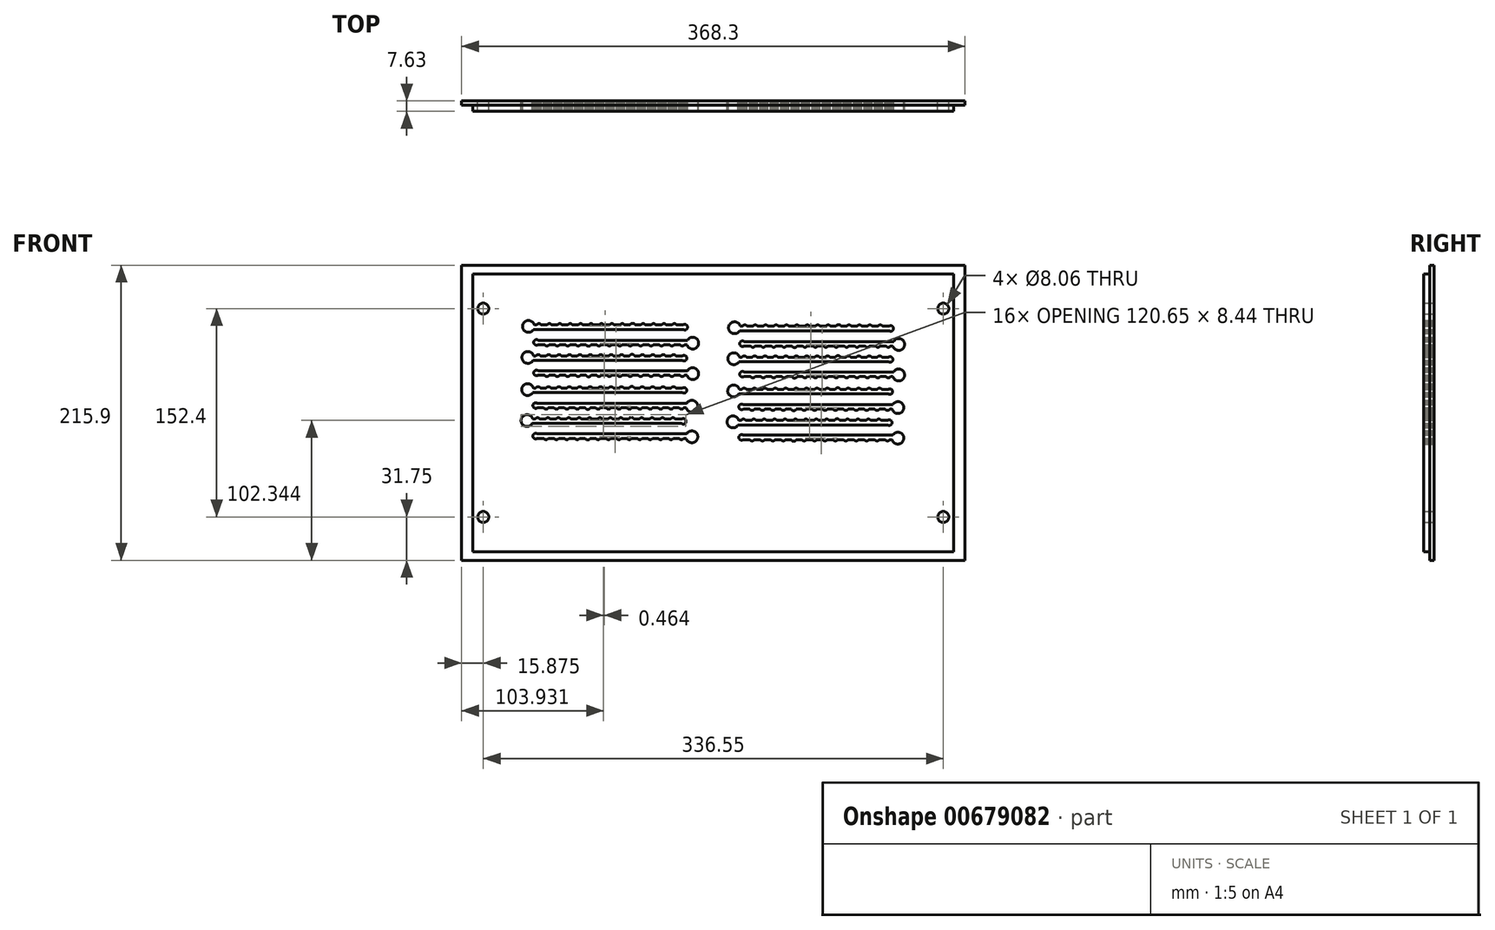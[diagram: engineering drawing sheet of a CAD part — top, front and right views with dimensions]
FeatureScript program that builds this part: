
annotation { "Feature Type Name" : "Feature", "Feature Type Description" : "" }
export const myFeature = defineFeature(function(context is Context, id is Id, definition is map)
    precondition{}
    {
        {
            var Q0;
            Q0=qCreatedBy(makeId("Front.planeOp"),FACE);
            var sketch = newSketch(context, id + "F0", { "sketchPlane" : qUnion([Q0])});
            skLineSegment(sketch, "E0.bottom", {"start": v(-184.15, 107.95) * mm, "end": v(184.15, 107.95) * mm});
            skLineSegment(sketch, "E0.top", {"start": v(-184.15, -107.95) * mm, "end": v(184.15, -107.95) * mm});
            skLineSegment(sketch, "E0.left", {"start": v(-184.15, 107.95) * mm, "end": v(-184.15, -107.95) * mm});
            skLineSegment(sketch, "E0.right", {"start": v(184.15, 107.95) * mm, "end": v(184.15, -107.95) * mm});
            skLineSegment(sketch, "E1.bottom", {"start": v(-175.9, 101.6) * mm, "end": v(175.9, 101.6) * mm});
            skLineSegment(sketch, "E1.top", {"start": v(-175.9, -101.6) * mm, "end": v(175.9, -101.6) * mm});
            skLineSegment(sketch, "E1.left", {"start": v(-175.9, 101.6) * mm, "end": v(-175.9, -101.6) * mm});
            skLineSegment(sketch, "E1.right", {"start": v(175.9, 101.6) * mm, "end": v(175.9, -101.6) * mm});
            skCircle(sketch, "E2", {"center": v(168.28, 76.2) * mm, "radius": 4.03 * mm});
            skCircle(sketch, "E3", {"center": v(168.28, -76.2) * mm, "radius": 4.03 * mm});
            skCircle(sketch, "E4", {"center": v(-168.28, -76.2) * mm, "radius": 4.03 * mm});
            skCircle(sketch, "E5", {"center": v(-168.28, 76.2) * mm, "radius": 4.03 * mm});
            skCircle(sketch, "E6", {"center": v(135.65, 50) * mm, "radius": 4.34 * mm});
            skCircle(sketch, "E7", {"center": v(128.03, 50) * mm, "radius": 2.05 * mm});
            skCircle(sketch, "E8", {"center": v(120.4, 50) * mm, "radius": 2.05 * mm});
            skCircle(sketch, "E9", {"center": v(112.79, 50) * mm, "radius": 2.05 * mm});
            skCircle(sketch, "E10", {"center": v(105.17, 50) * mm, "radius": 2.05 * mm});
            skCircle(sketch, "E11", {"center": v(97.55, 50) * mm, "radius": 2.05 * mm});
            skCircle(sketch, "E12", {"center": v(89.93, 50) * mm, "radius": 2.05 * mm});
            skCircle(sketch, "E13", {"center": v(82.3, 50) * mm, "radius": 2.05 * mm});
            skCircle(sketch, "E14", {"center": v(74.69, 50) * mm, "radius": 2.05 * mm});
            skCircle(sketch, "E15", {"center": v(67.07, 50) * mm, "radius": 2.05 * mm});
            skCircle(sketch, "E16", {"center": v(59.45, 49.73) * mm, "radius": 2.05 * mm});
            skCircle(sketch, "E17", {"center": v(51.83, 50) * mm, "radius": 2.05 * mm});
            skCircle(sketch, "E18", {"center": v(44.2, 50) * mm, "radius": 2.05 * mm});
            skCircle(sketch, "E19", {"center": v(36.59, 50) * mm, "radius": 2.05 * mm});
            skCircle(sketch, "E20", {"center": v(28.97, 50) * mm, "radius": 2.05 * mm});
            skCircle(sketch, "E21", {"center": v(21.35, 50.53) * mm, "radius": 2.05 * mm});
            skLineSegment(sketch, "E22", {"start": v(139.85, 48.92) * mm, "end": v(20.08, 48.92) * mm});
            skLineSegment(sketch, "E23", {"start": v(20.08, 48.92) * mm, "end": v(20.08, 52.14) * mm});
            skLineSegment(sketch, "E24", {"start": v(20.08, 52.14) * mm, "end": v(139.42, 52.14) * mm});
            skLineSegment(sketch, "E25", {"start": v(139.42, 52.14) * mm, "end": v(139.85, 48.92) * mm});
            skCircle(sketch, "E26", {"center": v(15.03, 39.53) * mm, "radius": 4.34 * mm});
            skCircle(sketch, "E27", {"center": v(22.65, 39.53) * mm, "radius": 2.05 * mm});
            skCircle(sketch, "E28", {"center": v(30.27, 39.53) * mm, "radius": 2.05 * mm});
            skCircle(sketch, "E29", {"center": v(37.89, 39.53) * mm, "radius": 2.05 * mm});
            skCircle(sketch, "E30", {"center": v(45.5, 39.53) * mm, "radius": 2.05 * mm});
            skCircle(sketch, "E31", {"center": v(53.13, 39.53) * mm, "radius": 2.05 * mm});
            skCircle(sketch, "E32", {"center": v(60.75, 39.53) * mm, "radius": 2.05 * mm});
            skCircle(sketch, "E33", {"center": v(68.37, 39.53) * mm, "radius": 2.05 * mm});
            skCircle(sketch, "E34", {"center": v(75.99, 39.53) * mm, "radius": 2.05 * mm});
            skCircle(sketch, "E35", {"center": v(83.6, 39.53) * mm, "radius": 2.05 * mm});
            skCircle(sketch, "E36", {"center": v(91.23, 39.8) * mm, "radius": 2.05 * mm});
            skCircle(sketch, "E37", {"center": v(98.85, 39.53) * mm, "radius": 2.05 * mm});
            skCircle(sketch, "E38", {"center": v(106.47, 39.53) * mm, "radius": 2.05 * mm});
            skCircle(sketch, "E39", {"center": v(114.09, 39.53) * mm, "radius": 2.05 * mm});
            skCircle(sketch, "E40", {"center": v(121.7, 39.53) * mm, "radius": 2.05 * mm});
            skCircle(sketch, "E41", {"center": v(129.33, 39) * mm, "radius": 2.05 * mm});
            skLineSegment(sketch, "E42", {"start": v(10.83, 40.61) * mm, "end": v(130.6, 40.61) * mm});
            skLineSegment(sketch, "E43", {"start": v(130.6, 40.61) * mm, "end": v(130.6, 37.39) * mm});
            skLineSegment(sketch, "E44", {"start": v(130.6, 37.39) * mm, "end": v(11.26, 37.39) * mm});
            skLineSegment(sketch, "E45", {"start": v(11.26, 37.39) * mm, "end": v(10.83, 40.61) * mm});
            skCircle(sketch, "E46", {"center": v(135.65, 27.67) * mm, "radius": 4.34 * mm});
            skCircle(sketch, "E47", {"center": v(128.03, 27.67) * mm, "radius": 2.05 * mm});
            skCircle(sketch, "E48", {"center": v(120.4, 27.67) * mm, "radius": 2.05 * mm});
            skCircle(sketch, "E49", {"center": v(112.79, 27.67) * mm, "radius": 2.05 * mm});
            skCircle(sketch, "E50", {"center": v(105.17, 27.67) * mm, "radius": 2.05 * mm});
            skCircle(sketch, "E51", {"center": v(97.55, 27.67) * mm, "radius": 2.05 * mm});
            skCircle(sketch, "E52", {"center": v(89.93, 27.67) * mm, "radius": 2.05 * mm});
            skCircle(sketch, "E53", {"center": v(82.3, 27.67) * mm, "radius": 2.05 * mm});
            skCircle(sketch, "E54", {"center": v(74.69, 27.67) * mm, "radius": 2.05 * mm});
            skCircle(sketch, "E55", {"center": v(67.07, 27.67) * mm, "radius": 2.05 * mm});
            skCircle(sketch, "E56", {"center": v(59.45, 27.4) * mm, "radius": 2.05 * mm});
            skCircle(sketch, "E57", {"center": v(51.83, 27.67) * mm, "radius": 2.05 * mm});
            skCircle(sketch, "E58", {"center": v(44.2, 27.67) * mm, "radius": 2.05 * mm});
            skCircle(sketch, "E59", {"center": v(36.59, 27.67) * mm, "radius": 2.05 * mm});
            skCircle(sketch, "E60", {"center": v(28.97, 27.67) * mm, "radius": 2.05 * mm});
            skCircle(sketch, "E61", {"center": v(21.35, 28.2) * mm, "radius": 2.05 * mm});
            skLineSegment(sketch, "E62", {"start": v(139.85, 26.59) * mm, "end": v(20.08, 26.59) * mm});
            skLineSegment(sketch, "E63", {"start": v(20.08, 26.59) * mm, "end": v(20.08, 29.8) * mm});
            skLineSegment(sketch, "E64", {"start": v(20.08, 29.8) * mm, "end": v(139.42, 29.8) * mm});
            skLineSegment(sketch, "E65", {"start": v(139.42, 29.8) * mm, "end": v(139.85, 26.59) * mm});
            skCircle(sketch, "E66", {"center": v(15.5, 62.2) * mm, "radius": 4.34 * mm});
            skCircle(sketch, "E67", {"center": v(23.11, 62.2) * mm, "radius": 2.05 * mm});
            skCircle(sketch, "E68", {"center": v(30.73, 62.2) * mm, "radius": 2.05 * mm});
            skCircle(sketch, "E69", {"center": v(38.35, 62.2) * mm, "radius": 2.05 * mm});
            skCircle(sketch, "E70", {"center": v(45.97, 62.2) * mm, "radius": 2.05 * mm});
            skCircle(sketch, "E71", {"center": v(53.6, 62.2) * mm, "radius": 2.05 * mm});
            skCircle(sketch, "E72", {"center": v(61.21, 62.2) * mm, "radius": 2.05 * mm});
            skCircle(sketch, "E73", {"center": v(68.83, 62.2) * mm, "radius": 2.05 * mm});
            skCircle(sketch, "E74", {"center": v(76.45, 62.2) * mm, "radius": 2.05 * mm});
            skCircle(sketch, "E75", {"center": v(84.07, 62.2) * mm, "radius": 2.05 * mm});
            skCircle(sketch, "E76", {"center": v(91.7, 62.47) * mm, "radius": 2.05 * mm});
            skCircle(sketch, "E77", {"center": v(99.31, 62.2) * mm, "radius": 2.05 * mm});
            skCircle(sketch, "E78", {"center": v(106.93, 62.2) * mm, "radius": 2.05 * mm});
            skCircle(sketch, "E79", {"center": v(114.55, 62.2) * mm, "radius": 2.05 * mm});
            skCircle(sketch, "E80", {"center": v(122.17, 62.2) * mm, "radius": 2.05 * mm});
            skCircle(sketch, "E81", {"center": v(129.8, 61.67) * mm, "radius": 2.05 * mm});
            skLineSegment(sketch, "E82", {"start": v(11.3, 63.28) * mm, "end": v(131.06, 63.28) * mm});
            skLineSegment(sketch, "E83", {"start": v(131.06, 63.28) * mm, "end": v(131.06, 60.06) * mm});
            skLineSegment(sketch, "E84", {"start": v(131.06, 60.06) * mm, "end": v(11.72, 60.06) * mm});
            skLineSegment(sketch, "E85", {"start": v(11.72, 60.06) * mm, "end": v(11.3, 63.28) * mm});
            skCircle(sketch, "E86", {"center": v(135.05, 3.79) * mm, "radius": 4.34 * mm});
            skCircle(sketch, "E87", {"center": v(127.43, 3.79) * mm, "radius": 2.05 * mm});
            skCircle(sketch, "E88", {"center": v(119.8, 3.79) * mm, "radius": 2.05 * mm});
            skCircle(sketch, "E89", {"center": v(112.19, 3.79) * mm, "radius": 2.05 * mm});
            skCircle(sketch, "E90", {"center": v(104.57, 3.79) * mm, "radius": 2.05 * mm});
            skCircle(sketch, "E91", {"center": v(96.95, 3.79) * mm, "radius": 2.05 * mm});
            skCircle(sketch, "E92", {"center": v(89.33, 3.79) * mm, "radius": 2.05 * mm});
            skCircle(sketch, "E93", {"center": v(81.7, 3.79) * mm, "radius": 2.05 * mm});
            skCircle(sketch, "E94", {"center": v(74.09, 3.79) * mm, "radius": 2.05 * mm});
            skCircle(sketch, "E95", {"center": v(66.47, 3.79) * mm, "radius": 2.05 * mm});
            skCircle(sketch, "E96", {"center": v(58.85, 3.52) * mm, "radius": 2.05 * mm});
            skCircle(sketch, "E97", {"center": v(51.23, 3.79) * mm, "radius": 2.05 * mm});
            skCircle(sketch, "E98", {"center": v(43.6, 3.79) * mm, "radius": 2.05 * mm});
            skCircle(sketch, "E99", {"center": v(35.99, 3.79) * mm, "radius": 2.05 * mm});
            skCircle(sketch, "E100", {"center": v(28.37, 3.79) * mm, "radius": 2.05 * mm});
            skCircle(sketch, "E101", {"center": v(20.75, 4.32) * mm, "radius": 2.05 * mm});
            skLineSegment(sketch, "E102", {"start": v(139.25, 2.71) * mm, "end": v(19.47, 2.71) * mm});
            skLineSegment(sketch, "E103", {"start": v(19.47, 2.71) * mm, "end": v(19.47, 5.93) * mm});
            skLineSegment(sketch, "E104", {"start": v(19.47, 5.93) * mm, "end": v(138.82, 5.93) * mm});
            skLineSegment(sketch, "E105", {"start": v(138.82, 5.93) * mm, "end": v(139.25, 2.71) * mm});
            skCircle(sketch, "E106", {"center": v(14.43, -6.68) * mm, "radius": 4.34 * mm});
            skCircle(sketch, "E107", {"center": v(22.05, -6.68) * mm, "radius": 2.05 * mm});
            skCircle(sketch, "E108", {"center": v(29.67, -6.68) * mm, "radius": 2.05 * mm});
            skCircle(sketch, "E109", {"center": v(37.29, -6.68) * mm, "radius": 2.05 * mm});
            skCircle(sketch, "E110", {"center": v(44.9, -6.68) * mm, "radius": 2.05 * mm});
            skCircle(sketch, "E111", {"center": v(52.53, -6.68) * mm, "radius": 2.05 * mm});
            skCircle(sketch, "E112", {"center": v(60.15, -6.68) * mm, "radius": 2.05 * mm});
            skCircle(sketch, "E113", {"center": v(67.77, -6.68) * mm, "radius": 2.05 * mm});
            skCircle(sketch, "E114", {"center": v(75.39, -6.68) * mm, "radius": 2.05 * mm});
            skCircle(sketch, "E115", {"center": v(83, -6.68) * mm, "radius": 2.05 * mm});
            skCircle(sketch, "E116", {"center": v(90.63, -6.4) * mm, "radius": 2.05 * mm});
            skCircle(sketch, "E117", {"center": v(98.25, -6.68) * mm, "radius": 2.05 * mm});
            skCircle(sketch, "E118", {"center": v(105.87, -6.68) * mm, "radius": 2.05 * mm});
            skCircle(sketch, "E119", {"center": v(113.49, -6.68) * mm, "radius": 2.05 * mm});
            skCircle(sketch, "E120", {"center": v(121.1, -6.68) * mm, "radius": 2.05 * mm});
            skCircle(sketch, "E121", {"center": v(128.73, -7.2) * mm, "radius": 2.05 * mm});
            skLineSegment(sketch, "E122", {"start": v(10.23, -5.6) * mm, "end": v(130, -5.6) * mm});
            skLineSegment(sketch, "E123", {"start": v(130, -5.6) * mm, "end": v(130, -8.82) * mm});
            skLineSegment(sketch, "E124", {"start": v(130, -8.82) * mm, "end": v(10.66, -8.82) * mm});
            skLineSegment(sketch, "E125", {"start": v(10.66, -8.82) * mm, "end": v(10.23, -5.6) * mm});
            skCircle(sketch, "E126", {"center": v(135.05, -18.54) * mm, "radius": 4.34 * mm});
            skCircle(sketch, "E127", {"center": v(127.43, -18.54) * mm, "radius": 2.05 * mm});
            skCircle(sketch, "E128", {"center": v(119.8, -18.54) * mm, "radius": 2.05 * mm});
            skCircle(sketch, "E129", {"center": v(112.19, -18.54) * mm, "radius": 2.05 * mm});
            skCircle(sketch, "E130", {"center": v(104.57, -18.54) * mm, "radius": 2.05 * mm});
            skCircle(sketch, "E131", {"center": v(96.95, -18.54) * mm, "radius": 2.05 * mm});
            skCircle(sketch, "E132", {"center": v(89.33, -18.54) * mm, "radius": 2.05 * mm});
            skCircle(sketch, "E133", {"center": v(81.7, -18.54) * mm, "radius": 2.05 * mm});
            skCircle(sketch, "E134", {"center": v(74.09, -18.54) * mm, "radius": 2.05 * mm});
            skCircle(sketch, "E135", {"center": v(66.47, -18.54) * mm, "radius": 2.05 * mm});
            skCircle(sketch, "E136", {"center": v(58.85, -18.8) * mm, "radius": 2.05 * mm});
            skCircle(sketch, "E137", {"center": v(51.23, -18.54) * mm, "radius": 2.05 * mm});
            skCircle(sketch, "E138", {"center": v(43.6, -18.54) * mm, "radius": 2.05 * mm});
            skCircle(sketch, "E139", {"center": v(35.99, -18.54) * mm, "radius": 2.05 * mm});
            skCircle(sketch, "E140", {"center": v(28.37, -18.54) * mm, "radius": 2.05 * mm});
            skCircle(sketch, "E141", {"center": v(20.75, -18) * mm, "radius": 2.05 * mm});
            skLineSegment(sketch, "E142", {"start": v(139.25, -19.62) * mm, "end": v(19.47, -19.62) * mm});
            skLineSegment(sketch, "E143", {"start": v(19.47, -19.62) * mm, "end": v(19.47, -16.4) * mm});
            skLineSegment(sketch, "E144", {"start": v(19.47, -16.4) * mm, "end": v(138.82, -16.4) * mm});
            skLineSegment(sketch, "E145", {"start": v(138.82, -16.4) * mm, "end": v(139.25, -19.62) * mm});
            skCircle(sketch, "E146", {"center": v(14.9, 16) * mm, "radius": 4.34 * mm});
            skCircle(sketch, "E147", {"center": v(22.51, 16) * mm, "radius": 2.05 * mm});
            skCircle(sketch, "E148", {"center": v(30.13, 16) * mm, "radius": 2.05 * mm});
            skCircle(sketch, "E149", {"center": v(37.75, 16) * mm, "radius": 2.05 * mm});
            skCircle(sketch, "E150", {"center": v(45.37, 16) * mm, "radius": 2.05 * mm});
            skCircle(sketch, "E151", {"center": v(53, 16) * mm, "radius": 2.05 * mm});
            skCircle(sketch, "E152", {"center": v(60.61, 16) * mm, "radius": 2.05 * mm});
            skCircle(sketch, "E153", {"center": v(68.23, 16) * mm, "radius": 2.05 * mm});
            skCircle(sketch, "E154", {"center": v(75.85, 16) * mm, "radius": 2.05 * mm});
            skCircle(sketch, "E155", {"center": v(83.47, 16) * mm, "radius": 2.05 * mm});
            skCircle(sketch, "E156", {"center": v(91.1, 16.26) * mm, "radius": 2.05 * mm});
            skCircle(sketch, "E157", {"center": v(98.71, 16) * mm, "radius": 2.05 * mm});
            skCircle(sketch, "E158", {"center": v(106.33, 16) * mm, "radius": 2.05 * mm});
            skCircle(sketch, "E159", {"center": v(113.95, 16) * mm, "radius": 2.05 * mm});
            skCircle(sketch, "E160", {"center": v(121.57, 16) * mm, "radius": 2.05 * mm});
            skCircle(sketch, "E161", {"center": v(129.2, 15.47) * mm, "radius": 2.05 * mm});
            skLineSegment(sketch, "E162", {"start": v(10.7, 17.08) * mm, "end": v(130.46, 17.08) * mm});
            skLineSegment(sketch, "E163", {"start": v(130.46, 17.08) * mm, "end": v(130.46, 13.86) * mm});
            skLineSegment(sketch, "E164", {"start": v(130.46, 13.86) * mm, "end": v(11.12, 13.86) * mm});
            skLineSegment(sketch, "E165", {"start": v(11.12, 13.86) * mm, "end": v(10.7, 17.08) * mm});
            skCircle(sketch, "E166", {"center": v(-15.03, 50.96) * mm, "radius": 4.34 * mm});
            skCircle(sketch, "E167", {"center": v(-22.65, 50.96) * mm, "radius": 2.05 * mm});
            skCircle(sketch, "E168", {"center": v(-30.27, 50.96) * mm, "radius": 2.05 * mm});
            skCircle(sketch, "E169", {"center": v(-37.89, 50.96) * mm, "radius": 2.05 * mm});
            skCircle(sketch, "E170", {"center": v(-45.5, 50.96) * mm, "radius": 2.05 * mm});
            skCircle(sketch, "E171", {"center": v(-53.13, 50.96) * mm, "radius": 2.05 * mm});
            skCircle(sketch, "E172", {"center": v(-60.75, 50.96) * mm, "radius": 2.05 * mm});
            skCircle(sketch, "E173", {"center": v(-68.37, 50.96) * mm, "radius": 2.05 * mm});
            skCircle(sketch, "E174", {"center": v(-75.99, 50.96) * mm, "radius": 2.05 * mm});
            skCircle(sketch, "E175", {"center": v(-83.6, 50.96) * mm, "radius": 2.05 * mm});
            skCircle(sketch, "E176", {"center": v(-91.23, 50.7) * mm, "radius": 2.05 * mm});
            skCircle(sketch, "E177", {"center": v(-98.85, 50.96) * mm, "radius": 2.05 * mm});
            skCircle(sketch, "E178", {"center": v(-106.47, 50.96) * mm, "radius": 2.05 * mm});
            skCircle(sketch, "E179", {"center": v(-114.09, 50.96) * mm, "radius": 2.05 * mm});
            skCircle(sketch, "E180", {"center": v(-121.7, 50.96) * mm, "radius": 2.05 * mm});
            skCircle(sketch, "E181", {"center": v(-129.33, 51.49) * mm, "radius": 2.05 * mm});
            skLineSegment(sketch, "E182", {"start": v(-10.83, 49.88) * mm, "end": v(-130.6, 49.88) * mm});
            skLineSegment(sketch, "E183", {"start": v(-130.6, 49.88) * mm, "end": v(-130.6, 53.1) * mm});
            skLineSegment(sketch, "E184", {"start": v(-130.6, 53.1) * mm, "end": v(-11.26, 53.1) * mm});
            skLineSegment(sketch, "E185", {"start": v(-11.26, 53.1) * mm, "end": v(-10.83, 49.88) * mm});
            skCircle(sketch, "E186", {"center": v(-135.64, 40.5) * mm, "radius": 4.34 * mm});
            skCircle(sketch, "E187", {"center": v(-128.02, 40.5) * mm, "radius": 2.05 * mm});
            skCircle(sketch, "E188", {"center": v(-120.4, 40.5) * mm, "radius": 2.05 * mm});
            skCircle(sketch, "E189", {"center": v(-112.78, 40.5) * mm, "radius": 2.05 * mm});
            skCircle(sketch, "E190", {"center": v(-105.16, 40.5) * mm, "radius": 2.05 * mm});
            skCircle(sketch, "E191", {"center": v(-97.54, 40.5) * mm, "radius": 2.05 * mm});
            skCircle(sketch, "E192", {"center": v(-89.92, 40.5) * mm, "radius": 2.05 * mm});
            skCircle(sketch, "E193", {"center": v(-82.3, 40.5) * mm, "radius": 2.05 * mm});
            skCircle(sketch, "E194", {"center": v(-74.68, 40.5) * mm, "radius": 2.05 * mm});
            skCircle(sketch, "E195", {"center": v(-67.06, 40.5) * mm, "radius": 2.05 * mm});
            skCircle(sketch, "E196", {"center": v(-59.44, 40.76) * mm, "radius": 2.05 * mm});
            skCircle(sketch, "E197", {"center": v(-51.82, 40.5) * mm, "radius": 2.05 * mm});
            skCircle(sketch, "E198", {"center": v(-44.2, 40.5) * mm, "radius": 2.05 * mm});
            skCircle(sketch, "E199", {"center": v(-36.58, 40.5) * mm, "radius": 2.05 * mm});
            skCircle(sketch, "E200", {"center": v(-28.96, 40.5) * mm, "radius": 2.05 * mm});
            skCircle(sketch, "E201", {"center": v(-21.34, 39.96) * mm, "radius": 2.05 * mm});
            skLineSegment(sketch, "E202", {"start": v(-139.85, 41.57) * mm, "end": v(-20.07, 41.57) * mm});
            skLineSegment(sketch, "E203", {"start": v(-20.07, 41.57) * mm, "end": v(-20.07, 38.35) * mm});
            skLineSegment(sketch, "E204", {"start": v(-20.07, 38.35) * mm, "end": v(-139.42, 38.35) * mm});
            skLineSegment(sketch, "E205", {"start": v(-139.42, 38.35) * mm, "end": v(-139.85, 41.57) * mm});
            skCircle(sketch, "E206", {"center": v(-15.03, 28.63) * mm, "radius": 4.34 * mm});
            skCircle(sketch, "E207", {"center": v(-22.65, 28.63) * mm, "radius": 2.05 * mm});
            skCircle(sketch, "E208", {"center": v(-30.27, 28.63) * mm, "radius": 2.05 * mm});
            skCircle(sketch, "E209", {"center": v(-37.89, 28.63) * mm, "radius": 2.05 * mm});
            skCircle(sketch, "E210", {"center": v(-45.5, 28.63) * mm, "radius": 2.05 * mm});
            skCircle(sketch, "E211", {"center": v(-53.13, 28.63) * mm, "radius": 2.05 * mm});
            skCircle(sketch, "E212", {"center": v(-60.75, 28.63) * mm, "radius": 2.05 * mm});
            skCircle(sketch, "E213", {"center": v(-68.37, 28.63) * mm, "radius": 2.05 * mm});
            skCircle(sketch, "E214", {"center": v(-75.99, 28.63) * mm, "radius": 2.05 * mm});
            skCircle(sketch, "E215", {"center": v(-83.6, 28.63) * mm, "radius": 2.05 * mm});
            skCircle(sketch, "E216", {"center": v(-91.23, 28.36) * mm, "radius": 2.05 * mm});
            skCircle(sketch, "E217", {"center": v(-98.85, 28.63) * mm, "radius": 2.05 * mm});
            skCircle(sketch, "E218", {"center": v(-106.47, 28.63) * mm, "radius": 2.05 * mm});
            skCircle(sketch, "E219", {"center": v(-114.09, 28.63) * mm, "radius": 2.05 * mm});
            skCircle(sketch, "E220", {"center": v(-121.7, 28.63) * mm, "radius": 2.05 * mm});
            skCircle(sketch, "E221", {"center": v(-129.33, 29.16) * mm, "radius": 2.05 * mm});
            skLineSegment(sketch, "E222", {"start": v(-10.83, 27.55) * mm, "end": v(-130.6, 27.55) * mm});
            skLineSegment(sketch, "E223", {"start": v(-130.6, 27.55) * mm, "end": v(-130.6, 30.77) * mm});
            skLineSegment(sketch, "E224", {"start": v(-130.6, 30.77) * mm, "end": v(-11.26, 30.77) * mm});
            skLineSegment(sketch, "E225", {"start": v(-11.26, 30.77) * mm, "end": v(-10.83, 27.55) * mm});
            skCircle(sketch, "E226", {"center": v(-135.18, 63.17) * mm, "radius": 4.34 * mm});
            skCircle(sketch, "E227", {"center": v(-127.56, 63.17) * mm, "radius": 2.05 * mm});
            skCircle(sketch, "E228", {"center": v(-119.94, 63.17) * mm, "radius": 2.05 * mm});
            skCircle(sketch, "E229", {"center": v(-112.32, 63.17) * mm, "radius": 2.05 * mm});
            skCircle(sketch, "E230", {"center": v(-104.7, 63.17) * mm, "radius": 2.05 * mm});
            skCircle(sketch, "E231", {"center": v(-97.08, 63.17) * mm, "radius": 2.05 * mm});
            skCircle(sketch, "E232", {"center": v(-89.46, 63.17) * mm, "radius": 2.05 * mm});
            skCircle(sketch, "E233", {"center": v(-81.84, 63.17) * mm, "radius": 2.05 * mm});
            skCircle(sketch, "E234", {"center": v(-74.22, 63.17) * mm, "radius": 2.05 * mm});
            skCircle(sketch, "E235", {"center": v(-66.6, 63.17) * mm, "radius": 2.05 * mm});
            skCircle(sketch, "E236", {"center": v(-58.98, 63.43) * mm, "radius": 2.05 * mm});
            skCircle(sketch, "E237", {"center": v(-51.36, 63.17) * mm, "radius": 2.05 * mm});
            skCircle(sketch, "E238", {"center": v(-43.74, 63.17) * mm, "radius": 2.05 * mm});
            skCircle(sketch, "E239", {"center": v(-36.12, 63.17) * mm, "radius": 2.05 * mm});
            skCircle(sketch, "E240", {"center": v(-28.5, 63.17) * mm, "radius": 2.05 * mm});
            skCircle(sketch, "E241", {"center": v(-20.88, 62.63) * mm, "radius": 2.05 * mm});
            skLineSegment(sketch, "E242", {"start": v(-139.38, 64.24) * mm, "end": v(-19.61, 64.24) * mm});
            skLineSegment(sketch, "E243", {"start": v(-19.61, 64.24) * mm, "end": v(-19.61, 61.02) * mm});
            skLineSegment(sketch, "E244", {"start": v(-19.61, 61.02) * mm, "end": v(-138.95, 61.02) * mm});
            skLineSegment(sketch, "E245", {"start": v(-138.95, 61.02) * mm, "end": v(-139.38, 64.24) * mm});
            skCircle(sketch, "E246", {"center": v(-15.63, 4.75) * mm, "radius": 4.34 * mm});
            skCircle(sketch, "E247", {"center": v(-23.25, 4.75) * mm, "radius": 2.05 * mm});
            skCircle(sketch, "E248", {"center": v(-30.87, 4.75) * mm, "radius": 2.05 * mm});
            skCircle(sketch, "E249", {"center": v(-38.49, 4.75) * mm, "radius": 2.05 * mm});
            skCircle(sketch, "E250", {"center": v(-46.1, 4.75) * mm, "radius": 2.05 * mm});
            skCircle(sketch, "E251", {"center": v(-53.73, 4.75) * mm, "radius": 2.05 * mm});
            skCircle(sketch, "E252", {"center": v(-61.35, 4.75) * mm, "radius": 2.05 * mm});
            skCircle(sketch, "E253", {"center": v(-68.97, 4.75) * mm, "radius": 2.05 * mm});
            skCircle(sketch, "E254", {"center": v(-76.59, 4.75) * mm, "radius": 2.05 * mm});
            skCircle(sketch, "E255", {"center": v(-84.2, 4.75) * mm, "radius": 2.05 * mm});
            skCircle(sketch, "E256", {"center": v(-91.83, 4.48) * mm, "radius": 2.05 * mm});
            skCircle(sketch, "E257", {"center": v(-99.45, 4.75) * mm, "radius": 2.05 * mm});
            skCircle(sketch, "E258", {"center": v(-107.07, 4.75) * mm, "radius": 2.05 * mm});
            skCircle(sketch, "E259", {"center": v(-114.69, 4.75) * mm, "radius": 2.05 * mm});
            skCircle(sketch, "E260", {"center": v(-122.3, 4.75) * mm, "radius": 2.05 * mm});
            skCircle(sketch, "E261", {"center": v(-129.93, 5.28) * mm, "radius": 2.05 * mm});
            skLineSegment(sketch, "E262", {"start": v(-11.43, 3.67) * mm, "end": v(-131.2, 3.67) * mm});
            skLineSegment(sketch, "E263", {"start": v(-131.2, 3.67) * mm, "end": v(-131.2, 6.9) * mm});
            skLineSegment(sketch, "E264", {"start": v(-131.2, 6.9) * mm, "end": v(-11.86, 6.9) * mm});
            skLineSegment(sketch, "E265", {"start": v(-11.86, 6.9) * mm, "end": v(-11.43, 3.67) * mm});
            skCircle(sketch, "E266", {"center": v(-136.24, -5.72) * mm, "radius": 4.34 * mm});
            skCircle(sketch, "E267", {"center": v(-128.62, -5.72) * mm, "radius": 2.05 * mm});
            skCircle(sketch, "E268", {"center": v(-121, -5.72) * mm, "radius": 2.05 * mm});
            skCircle(sketch, "E269", {"center": v(-113.38, -5.72) * mm, "radius": 2.05 * mm});
            skCircle(sketch, "E270", {"center": v(-105.76, -5.72) * mm, "radius": 2.05 * mm});
            skCircle(sketch, "E271", {"center": v(-98.14, -5.72) * mm, "radius": 2.05 * mm});
            skCircle(sketch, "E272", {"center": v(-90.52, -5.72) * mm, "radius": 2.05 * mm});
            skCircle(sketch, "E273", {"center": v(-82.9, -5.72) * mm, "radius": 2.05 * mm});
            skCircle(sketch, "E274", {"center": v(-75.28, -5.72) * mm, "radius": 2.05 * mm});
            skCircle(sketch, "E275", {"center": v(-67.66, -5.72) * mm, "radius": 2.05 * mm});
            skCircle(sketch, "E276", {"center": v(-60.04, -5.45) * mm, "radius": 2.05 * mm});
            skCircle(sketch, "E277", {"center": v(-52.42, -5.72) * mm, "radius": 2.05 * mm});
            skCircle(sketch, "E278", {"center": v(-44.8, -5.72) * mm, "radius": 2.05 * mm});
            skCircle(sketch, "E279", {"center": v(-37.18, -5.72) * mm, "radius": 2.05 * mm});
            skCircle(sketch, "E280", {"center": v(-29.56, -5.72) * mm, "radius": 2.05 * mm});
            skCircle(sketch, "E281", {"center": v(-21.94, -6.25) * mm, "radius": 2.05 * mm});
            skLineSegment(sketch, "E282", {"start": v(-140.45, -4.64) * mm, "end": v(-20.67, -4.64) * mm});
            skLineSegment(sketch, "E283", {"start": v(-20.67, -4.64) * mm, "end": v(-20.67, -7.86) * mm});
            skLineSegment(sketch, "E284", {"start": v(-20.67, -7.86) * mm, "end": v(-140.02, -7.86) * mm});
            skLineSegment(sketch, "E285", {"start": v(-140.02, -7.86) * mm, "end": v(-140.45, -4.64) * mm});
            skCircle(sketch, "E286", {"center": v(-15.63, -17.58) * mm, "radius": 4.34 * mm});
            skCircle(sketch, "E287", {"center": v(-23.25, -17.58) * mm, "radius": 2.05 * mm});
            skCircle(sketch, "E288", {"center": v(-30.87, -17.58) * mm, "radius": 2.05 * mm});
            skCircle(sketch, "E289", {"center": v(-38.49, -17.58) * mm, "radius": 2.05 * mm});
            skCircle(sketch, "E290", {"center": v(-46.1, -17.58) * mm, "radius": 2.05 * mm});
            skCircle(sketch, "E291", {"center": v(-53.73, -17.58) * mm, "radius": 2.05 * mm});
            skCircle(sketch, "E292", {"center": v(-61.35, -17.58) * mm, "radius": 2.05 * mm});
            skCircle(sketch, "E293", {"center": v(-68.97, -17.58) * mm, "radius": 2.05 * mm});
            skCircle(sketch, "E294", {"center": v(-76.59, -17.58) * mm, "radius": 2.05 * mm});
            skCircle(sketch, "E295", {"center": v(-84.2, -17.58) * mm, "radius": 2.05 * mm});
            skCircle(sketch, "E296", {"center": v(-91.83, -17.85) * mm, "radius": 2.05 * mm});
            skCircle(sketch, "E297", {"center": v(-99.45, -17.58) * mm, "radius": 2.05 * mm});
            skCircle(sketch, "E298", {"center": v(-107.07, -17.58) * mm, "radius": 2.05 * mm});
            skCircle(sketch, "E299", {"center": v(-114.69, -17.58) * mm, "radius": 2.05 * mm});
            skCircle(sketch, "E300", {"center": v(-122.3, -17.58) * mm, "radius": 2.05 * mm});
            skCircle(sketch, "E301", {"center": v(-129.93, -17.05) * mm, "radius": 2.05 * mm});
            skLineSegment(sketch, "E302", {"start": v(-11.43, -18.66) * mm, "end": v(-131.2, -18.66) * mm});
            skLineSegment(sketch, "E303", {"start": v(-131.2, -18.66) * mm, "end": v(-131.2, -15.44) * mm});
            skLineSegment(sketch, "E304", {"start": v(-131.2, -15.44) * mm, "end": v(-11.86, -15.44) * mm});
            skLineSegment(sketch, "E305", {"start": v(-11.86, -15.44) * mm, "end": v(-11.43, -18.66) * mm});
            skCircle(sketch, "E306", {"center": v(-135.78, 16.96) * mm, "radius": 4.34 * mm});
            skCircle(sketch, "E307", {"center": v(-128.16, 16.96) * mm, "radius": 2.05 * mm});
            skCircle(sketch, "E308", {"center": v(-120.54, 16.96) * mm, "radius": 2.05 * mm});
            skCircle(sketch, "E309", {"center": v(-112.92, 16.96) * mm, "radius": 2.05 * mm});
            skCircle(sketch, "E310", {"center": v(-105.3, 16.96) * mm, "radius": 2.05 * mm});
            skCircle(sketch, "E311", {"center": v(-97.68, 16.96) * mm, "radius": 2.05 * mm});
            skCircle(sketch, "E312", {"center": v(-90.06, 16.96) * mm, "radius": 2.05 * mm});
            skCircle(sketch, "E313", {"center": v(-82.44, 16.96) * mm, "radius": 2.05 * mm});
            skCircle(sketch, "E314", {"center": v(-74.82, 16.96) * mm, "radius": 2.05 * mm});
            skCircle(sketch, "E315", {"center": v(-67.2, 16.96) * mm, "radius": 2.05 * mm});
            skCircle(sketch, "E316", {"center": v(-59.58, 17.22) * mm, "radius": 2.05 * mm});
            skCircle(sketch, "E317", {"center": v(-51.96, 16.96) * mm, "radius": 2.05 * mm});
            skCircle(sketch, "E318", {"center": v(-44.34, 16.96) * mm, "radius": 2.05 * mm});
            skCircle(sketch, "E319", {"center": v(-36.72, 16.96) * mm, "radius": 2.05 * mm});
            skCircle(sketch, "E320", {"center": v(-29.1, 16.96) * mm, "radius": 2.05 * mm});
            skCircle(sketch, "E321", {"center": v(-21.48, 16.43) * mm, "radius": 2.05 * mm});
            skLineSegment(sketch, "E322", {"start": v(-139.98, 18.04) * mm, "end": v(-20.21, 18.04) * mm});
            skLineSegment(sketch, "E323", {"start": v(-20.21, 18.04) * mm, "end": v(-20.21, 14.82) * mm});
            skLineSegment(sketch, "E324", {"start": v(-20.21, 14.82) * mm, "end": v(-139.55, 14.82) * mm});
            skLineSegment(sketch, "E325", {"start": v(-139.55, 14.82) * mm, "end": v(-139.98, 18.04) * mm});
            skSolve(sketch);
        }
        {
            var Q0;
            Q0=makeQuery(id+"F0.imprint","IMPRINT",FACE,{"disambiguationData":[TD([[makeQuery(id+"F0.imprint","IMPRINT",EDGE,{"derivedFrom":sQuery(id+"F0.wireOp",EDGE,"E1.bottom")}),-1.0]])]});
            extrude(context, id + "F1", {"entities" : qUnion([Q0]), "depth" : 4.44 * mm, "offsetDistance" : 25.4 * mm});
        }
        {
            var Q0;
            {var subQ0=sQuery(id+"F0.wireOp",EDGE,"E0.bottom");Q0=makeQuery(id+"F0.imprint","IMPRINT",FACE,{"disambiguationData":[TD([[makeQuery(id+"F0.imprint","IMPRINT",EDGE,{"derivedFrom":subQ0}),-1.0]])]});}
            var Q1;
            {var subQ0=sQuery(id+"F0.wireOp",EDGE,"E0.top");Q1=makeQuery(id+"F0.imprint","IMPRINT",FACE,{"disambiguationData":[TD([[makeQuery(id+"F0.imprint","IMPRINT",EDGE,{"derivedFrom":subQ0}),1.0]])]});}
            var Q2;
            Q2=makeQuery(id+"F0.imprint","IMPRINT",FACE,{"disambiguationData":[TD([[makeQuery(id+"F0.imprint","IMPRINT",EDGE,{"derivedFrom":sQuery(id+"F0.wireOp",EDGE,"E1.bottom")}),-1.0]])]});
            extrude(context, id + "F2", {"entities" : qUnion([Q0, Q1, Q2]), "operationType" : NewBodyOperationType.ADD, "depth" : -3.17 * mm, "offsetDistance" : 25.4 * mm});
        }
    });
